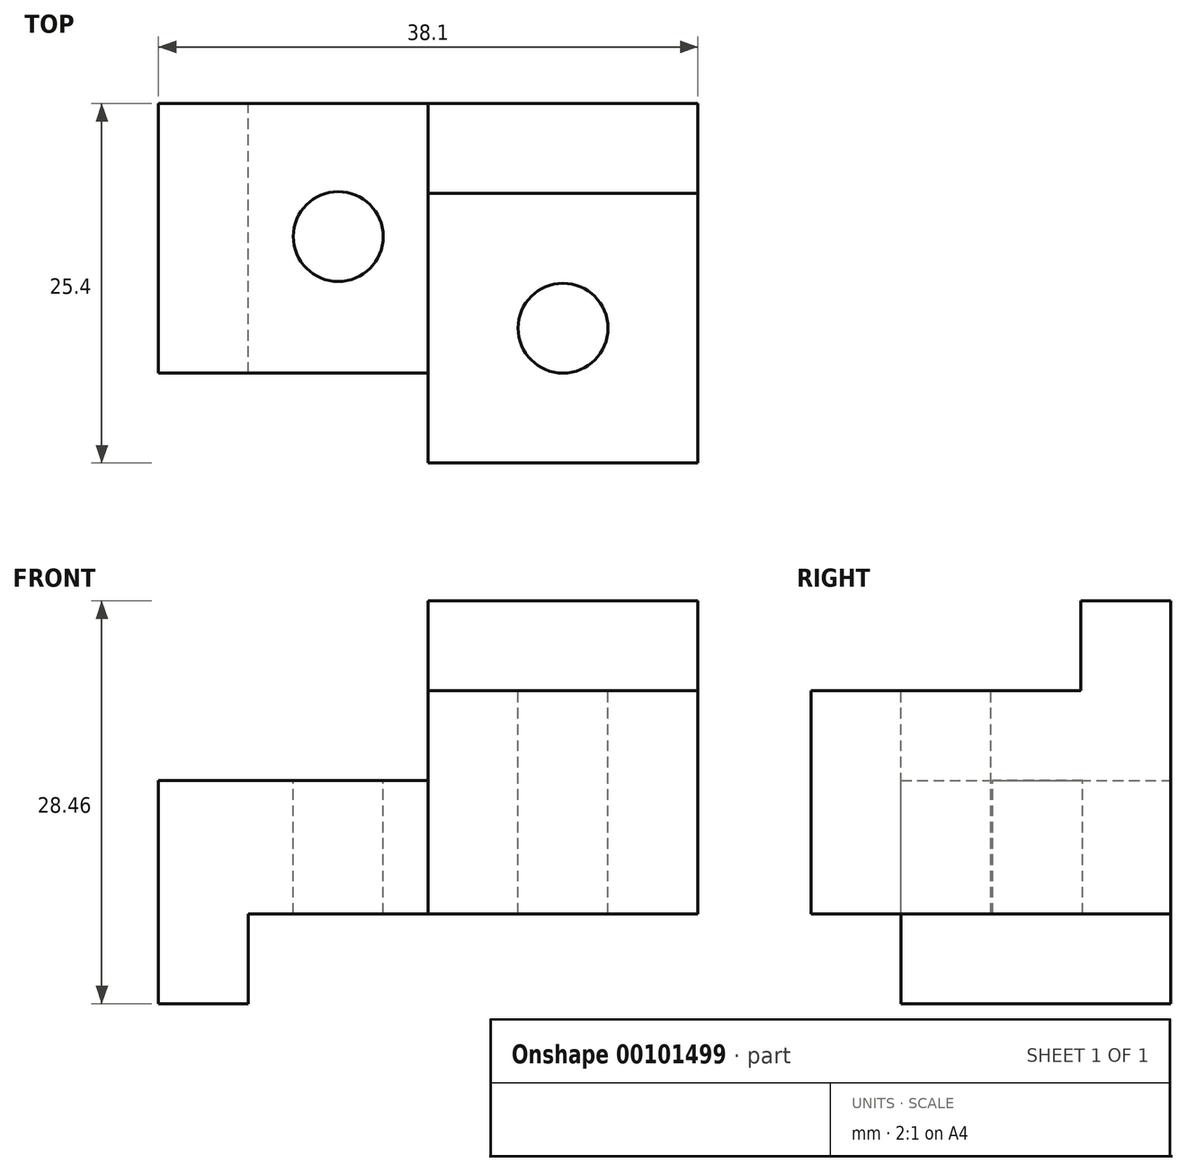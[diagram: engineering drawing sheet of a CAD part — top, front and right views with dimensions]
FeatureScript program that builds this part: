
annotation { "Feature Type Name" : "Feature", "Feature Type Description" : "" }
export const myFeature = defineFeature(function(context is Context, id is Id, definition is map)
    precondition{}
    {
        {
            var Q0;
            Q0=qCreatedBy(makeId("Front.planeOp"),FACE);
            var sketch = newSketch(context, id + "F0", { "sketchPlane" : qUnion([Q0])});
            skLineSegment(sketch, "E0", {"start": v(0, 0) * mm, "end": v(0, 15.76) * mm});
            skLineSegment(sketch, "E1", {"start": v(0, 15.76) * mm, "end": v(19.05, 15.76) * mm});
            skLineSegment(sketch, "E2", {"start": v(19.05, 15.76) * mm, "end": v(19.05, 28.46) * mm});
            skLineSegment(sketch, "E3", {"start": v(19.05, 28.46) * mm, "end": v(38.1, 28.46) * mm});
            skLineSegment(sketch, "E4", {"start": v(38.1, 28.46) * mm, "end": v(38.1, 6.35) * mm});
            skLineSegment(sketch, "E5", {"start": v(38.1, 6.35) * mm, "end": v(6.35, 6.35) * mm});
            skLineSegment(sketch, "E6", {"start": v(6.35, 6.35) * mm, "end": v(6.35, 0) * mm});
            skLineSegment(sketch, "E7", {"start": v(6.35, 0) * mm, "end": v(0, 0) * mm});
            skSolve(sketch);
        }
        {
            var Q0;
            Q0=makeQuery(id+"F0.imprint","IMPRINT",FACE,{"disambiguationData":[TD([[makeQuery(id+"F0.imprint","IMPRINT",EDGE,{"derivedFrom":sQuery(id+"F0.wireOp",EDGE,"E0")}),-1.0]])]});
            extrude(context, id + "F1", {"entities" : qUnion([Q0]), "depth" : 19.05 * mm});
        }
        {
            var Q0;
            Q0=makeQuery(id+"F1.opExtrude","CAP_FACE",FACE,{"disambiguationData":[OSD([sQuery(id+"F0.wireOp",EDGE,"E0"),sQuery(id+"F0.wireOp",EDGE,"E1"),sQuery(id+"F0.wireOp",EDGE,"E2"),sQuery(id+"F0.wireOp",EDGE,"E3"),sQuery(id+"F0.wireOp",EDGE,"E4"),sQuery(id+"F0.wireOp",EDGE,"E5"),sQuery(id+"F0.wireOp",EDGE,"E6"),sQuery(id+"F0.wireOp",EDGE,"E7")])],"isStart":false});
            var sketch = newSketch(context, id + "F2", { "sketchPlane" : qUnion([Q0])});
            skLineSegment(sketch, "E8", {"start": v(19.05, 28.46) * mm, "end": v(38.1, 28.46) * mm});
            skLineSegment(sketch, "E9", {"start": v(38.1, 28.46) * mm, "end": v(38.1, 6.35) * mm});
            skLineSegment(sketch, "E10", {"start": v(38.1, 6.35) * mm, "end": v(19.05, 6.35) * mm});
            skLineSegment(sketch, "E11", {"start": v(19.05, 28.46) * mm, "end": v(19.05, 6.35) * mm});
            skSolve(sketch);
        }
        {
            var Q0;
            {var subQ2=sQuery(id+"F2.wireOp",EDGE,"E8");Q0=makeQuery(id+"F2.imprint","IMPRINT",FACE,{"disambiguationData":[TD([[makeQuery(id+"F2.imprint","IMPRINT",EDGE,{"derivedFrom":subQ2}),-1.0]])]});}
            extrude(context, id + "F3", {"entities" : qUnion([Q0]), "operationType" : NewBodyOperationType.ADD, "depth" : 6.35 * mm});
        }
        {
            var Q0;
            Q0=makeQuery(id+"F3.boolean.opBoolean","MERGE",FACE,{"derivedFrom":[makeQuery(id+"F1.opExtrude","SWEPT_FACE",FACE,{"disambiguationData":[OSD([sQuery(id+"F0.wireOp",EDGE,"E4")])]}),makeQuery(id+"F3.opExtrude","SWEPT_FACE",FACE,{"disambiguationData":[OSD([sQuery(id+"F2.wireOp",EDGE,"E9")])]})]});
            var sketch = newSketch(context, id + "F4", { "sketchPlane" : qUnion([Q0])});
            skLineSegment(sketch, "E12", {"start": v(-25.4, 22.11) * mm, "end": v(-6.35, 22.11) * mm});
            skLineSegment(sketch, "E13", {"start": v(-6.35, 22.11) * mm, "end": v(-6.35, 28.46) * mm});
            skSolve(sketch);
        }
        {
            var Q0;
            {var subQ0=sQuery(id+"F4.wireOp",EDGE,"E12");Q0=makeQuery(id+"F4.imprint","IMPRINT",FACE,{"disambiguationData":[TD([[makeQuery(id+"F4.imprint","IMPRINT",EDGE,{"derivedFrom":subQ0}),1.0]])]});}
            extrude(context, id + "F5", {"entities" : qUnion([Q0]), "operationType" : NewBodyOperationType.REMOVE, "endBound" : BoundingType.THROUGH_ALL, "oppositeDirection" : true, "depth" : 25.4 * mm});
        }
        {
            var Q0;
            Q0=makeQuery(id+"F5.boolean.opBoolean","COPY",FACE,{"derivedFrom":makeQuery(id+"F5.opExtrude","SWEPT_FACE",FACE,{"disambiguationData":[OSD([sQuery(id+"F4.wireOp",EDGE,"E12")])]})});
            var sketch = newSketch(context, id + "F6", { "sketchPlane" : qUnion([Q0])});
            skCircle(sketch, "E14", {"center": v(28.58, -15.87) * mm, "radius": 3.18 * mm});
            skLineSegment(sketch, "E15", {"start": v(19.05, -6.35) * mm, "end": v(38.1, -25.4) * mm, "construction": true});
            skSolve(sketch);
        }
        {
            var Q0;
            Q0=makeQuery(id+"F6.imprint","IMPRINT",FACE,{"disambiguationData":[TD([[makeQuery(id+"F6.imprint","IMPRINT",EDGE,{"derivedFrom":sQuery(id+"F6.wireOp",EDGE,"E14")}),1.0]])]});
            extrude(context, id + "F7", {"entities" : qUnion([Q0]), "operationType" : NewBodyOperationType.REMOVE, "endBound" : BoundingType.THROUGH_ALL, "oppositeDirection" : true, "depth" : 25.4 * mm});
        }
        {
            var Q0;
            Q0=makeQuery(id+"F1.opExtrude","SWEPT_FACE",FACE,{"disambiguationData":[OSD([sQuery(id+"F0.wireOp",EDGE,"E1")])]});
            var sketch = newSketch(context, id + "F8", { "sketchPlane" : qUnion([Q0])});
            skCircle(sketch, "E16", {"center": v(12.7, -9.4) * mm, "radius": 3.18 * mm});
            skSolve(sketch);
        }
        {
            var Q0;
            Q0=makeQuery(id+"F8.imprint","IMPRINT",FACE,{"disambiguationData":[TD([[makeQuery(id+"F8.imprint","IMPRINT",EDGE,{"derivedFrom":sQuery(id+"F8.wireOp",EDGE,"E16")}),1.0]])]});
            extrude(context, id + "F9", {"entities" : qUnion([Q0]), "operationType" : NewBodyOperationType.REMOVE, "endBound" : BoundingType.THROUGH_ALL, "oppositeDirection" : true, "depth" : 25.4 * mm});
        }
    });
